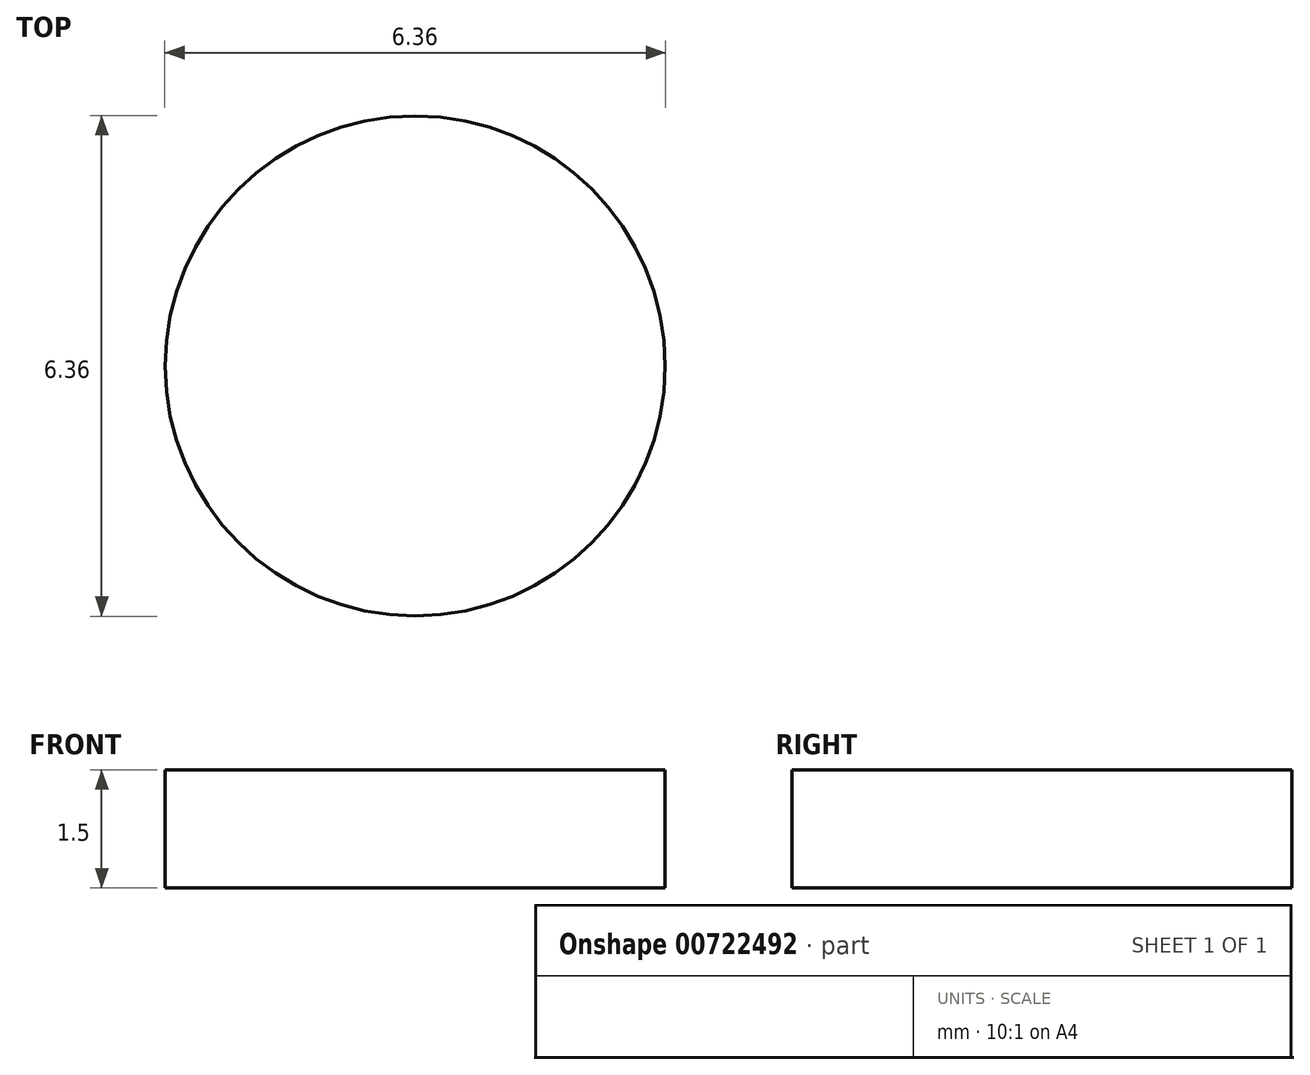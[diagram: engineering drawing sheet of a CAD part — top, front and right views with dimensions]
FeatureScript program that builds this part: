
annotation { "Feature Type Name" : "Feature", "Feature Type Description" : "" }
export const myFeature = defineFeature(function(context is Context, id is Id, definition is map)
    precondition{}
    {
        {
            assignVariable(context, id + "F0", {"name" : "T", "anyValue" : .75});
        }
        {
            var Q0;
            Q0=qCreatedBy(makeId("Top.planeOp"),FACE);
            var sketch = newSketch(context, id + "F1", { "sketchPlane" : qUnion([Q0])});
            skCircle(sketch, "E0", {"center": v(0, 0) * mm, "radius": 3.18 * mm});
            skSolve(sketch);
        }
        {
            var Q0;
            Q0 = qSketchRegion(id + "F1", true);
            extrude(context, id + "F2", {"entities" : qUnion([Q0]), "depth" : (getVariable(context, 'T') * 2) * mm, "offsetDistance" : 25.4 * mm});
        }
    });
